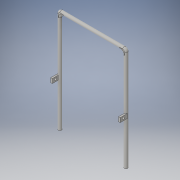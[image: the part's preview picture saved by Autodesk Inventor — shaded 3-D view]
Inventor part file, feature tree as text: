
AUTODESK INVENTOR PART (.ipt)
format: ipt  version: 2016 (Build 200138000, 138)  size: 152,064 bytes
history: native  units: in
note: dims shown in document units (in); Inventor stores cm internally (conversion verified against a paired STEP export)
features: sketch x3, extrude x2, fillet x1, hole x1
ambient origin geometry x8: Origin, YZ Plane, XZ Plane, XY Plane, X Axis, Y Axis, Z Axis, Center Point
bodies: Solid1 (feature_tree)
feature tree (7):
  extrude  "Extrusion1"  Depth=0.75in TaperAngle=0.0deg
  fillet  "Fillet1"  Radius=0.375in
  extrude  "Extrusion2"  Depth=1.0in
  sketch  "Sketch3"  dims[d15=0.375in d16=1.0in d17=10.0in d18=1.75in d19=0.0in d20=0.5in d21=0.75in d24=0.5in d25=0.75in d26=0.375in d27=0.25in d28=0.5635in d29=1.0in d30=0.0in d31=24.0in d32=24.0in d33=0.75in d34=15.25in]
  hole  "Hole1"  [1 undecoded]
  sketch  "Sketch1"  dims[d7=16.0in d8=0.75in d9=0.0in d10=0.375in]
  sketch  "Sketch2"  dims[d13=10.0in d14=1.0in]
note: 1 required parameter value undecoded (feature->parameter linkage not recoverable at this tier; creation-order binding heuristic only, values carry confidence <= 0.55)
